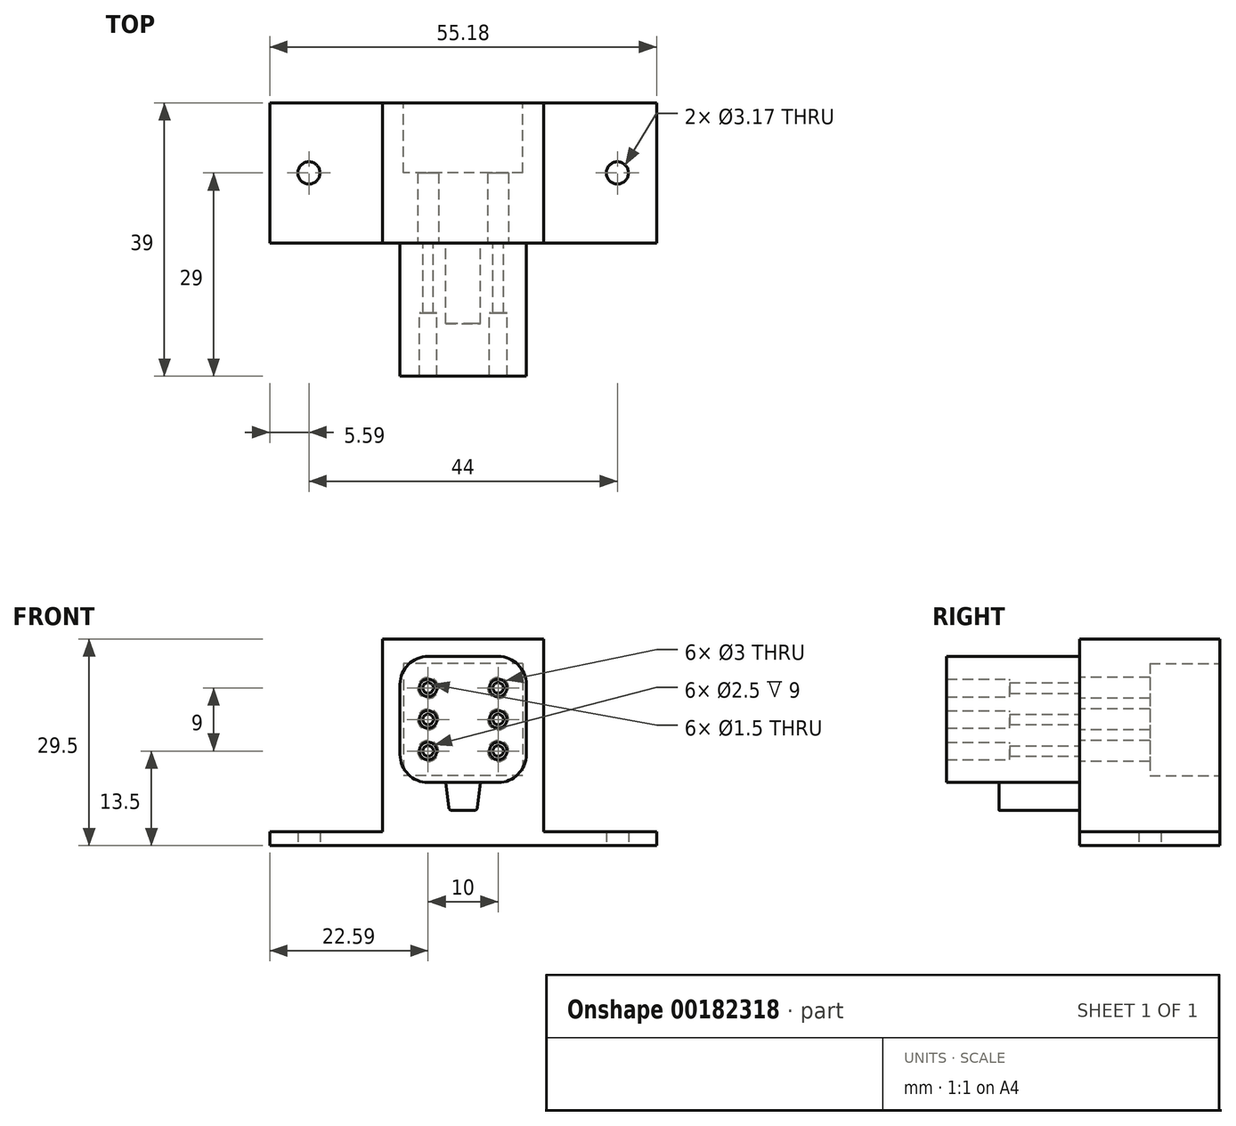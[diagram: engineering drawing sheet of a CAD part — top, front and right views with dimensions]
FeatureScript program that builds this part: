
annotation { "Feature Type Name" : "Feature", "Feature Type Description" : "" }
export const myFeature = defineFeature(function(context is Context, id is Id, definition is map)
    precondition{}
    {
        {
            var Q0;
            Q0=qCreatedBy(makeId("Front.planeOp"),FACE);
            var sketch = newSketch(context, id + "F0", { "sketchPlane" : qUnion([Q0])});
            skLineSegment(sketch, "E0.bottom", {"start": v(7.5, 30.5) * mm, "end": v(17.5, 30.5) * mm});
            skLineSegment(sketch, "E0.top", {"start": v(7.5, 12.5) * mm, "end": v(17.5, 12.5) * mm});
            skLineSegment(sketch, "E0.left", {"start": v(3.5, 26.5) * mm, "end": v(3.5, 16.5) * mm});
            skLineSegment(sketch, "E0.right", {"start": v(21.5, 26.5) * mm, "end": v(21.5, 16.5) * mm});
            skPoint(sketch, "E1.visualSharp", {"position": v(3.5, 30.5) * mm});
            skArc(sketch, "E1.filletArc", {"start": v(7.5, 30.5) * mm, "mid": v(4.67, 29.33) * mm, "end": v(3.5, 26.5) * mm});
            skPoint(sketch, "E2.visualSharp", {"position": v(21.5, 30.5) * mm});
            skArc(sketch, "E2.filletArc", {"start": v(21.5, 26.5) * mm, "mid": v(20.33, 29.33) * mm, "end": v(17.5, 30.5) * mm});
            skPoint(sketch, "E3.visualSharp", {"position": v(21.5, 12.5) * mm});
            skArc(sketch, "E3.filletArc", {"start": v(17.5, 12.5) * mm, "mid": v(20.33, 13.67) * mm, "end": v(21.5, 16.5) * mm});
            skPoint(sketch, "E4.visualSharp", {"position": v(3.5, 12.5) * mm});
            skArc(sketch, "E4.filletArc", {"start": v(3.5, 16.5) * mm, "mid": v(4.67, 13.67) * mm, "end": v(7.5, 12.5) * mm});
            skLineSegment(sketch, "E5", {"start": v(12.5, 30.5) * mm, "end": v(12.5, 6.08) * mm, "construction": true});
            skCircle(sketch, "E6", {"center": v(7.5, 26) * mm, "radius": 1.25 * mm});
            skLineSegment(sketch, "E7", {"start": v(7.5, 26) * mm, "end": v(12.5, 26) * mm, "construction": true});
            skCircle(sketch, "E8.1.0.0", {"center": v(7.5, 21.5) * mm, "radius": 1.25 * mm});
            skCircle(sketch, "E8.2.0.0", {"center": v(7.5, 17) * mm, "radius": 1.25 * mm});
            skLineSegment(sketch, "E8.direction1", {"start": v(7.5, 26) * mm, "end": v(7.5, 21.5) * mm, "construction": true});
            skCircle(sketch, "E9.MirrorC", {"center": v(17.5, 26) * mm, "radius": 1.25 * mm});
            skCircle(sketch, "E10.MirrorC", {"center": v(17.5, 21.5) * mm, "radius": 1.25 * mm});
            skCircle(sketch, "E11.MirrorC", {"center": v(17.5, 17) * mm, "radius": 1.25 * mm});
            skLineSegment(sketch, "E12.MirrorCS", {"start": v(17.5, 26) * mm, "end": v(17.5, 21.5) * mm, "construction": true});
            skSolve(sketch);
        }
        {
            var Q0;
            Q0=qSketchRegion(id+"F0",true);
            extrude(context, id + "F1", {"entities" : qUnion([Q0]), "depth" : 19 * mm});
        }
        {
            var Q0;
            Q0=makeQuery(id+"F1.opExtrude","CAP_FACE",FACE,{"disambiguationData":[OSD([sQuery(id+"F0.wireOp",EDGE,"E0.bottom"),sQuery(id+"F0.wireOp",EDGE,"E0.top"),sQuery(id+"F0.wireOp",EDGE,"E0.left"),sQuery(id+"F0.wireOp",EDGE,"E0.right"),sQuery(id+"F0.wireOp",EDGE,"E1.filletArc"),sQuery(id+"F0.wireOp",EDGE,"E2.filletArc"),sQuery(id+"F0.wireOp",EDGE,"E3.filletArc"),sQuery(id+"F0.wireOp",EDGE,"E4.filletArc"),sQuery(id+"F0.wireOp",EDGE,"6d2e094a-fbc0-4e1c-b2e7-ed02ba3bef07"),sQuery(id+"F0.wireOp",EDGE,"E6"),sQuery(id+"F0.wireOp",EDGE,"E8.1.0.0"),sQuery(id+"F0.wireOp",EDGE,"E8.2.0.0"),sQuery(id+"F0.wireOp",EDGE,"E9.MirrorC"),sQuery(id+"F0.wireOp",EDGE,"E10.MirrorC"),sQuery(id+"F0.wireOp",EDGE,"E11.MirrorC")])],"isStart":true});
            var sketch = newSketch(context, id + "F2", { "sketchPlane" : qUnion([Q0])});
            skLineSegment(sketch, "E13.bottom", {"start": v(-15, 12.5) * mm, "end": v(-10, 12.5) * mm});
            skPoint(sketch, "E14", {"position": v(-12.5, 12.5) * mm});
            skLineSegment(sketch, "E15", {"start": v(-15, 12.5) * mm, "end": v(-14.55, 8.94) * mm});
            skLineSegment(sketch, "E16", {"start": v(-14.06, 8.5) * mm, "end": v(-10.94, 8.5) * mm});
            skLineSegment(sketch, "E17", {"start": v(-10.45, 8.94) * mm, "end": v(-10, 12.5) * mm});
            skLineSegment(sketch, "E18", {"start": v(-12.5, 8.5) * mm, "end": v(-12.5, 12.5) * mm, "construction": true});
            skPoint(sketch, "E19.visualSharp", {"position": v(-14.5, 8.5) * mm});
            skArc(sketch, "E19.filletArc", {"start": v(-14.55, 8.94) * mm, "mid": v(-14.39, 8.63) * mm, "end": v(-14.06, 8.5) * mm});
            skPoint(sketch, "E20.visualSharp", {"position": v(-10.5, 8.5) * mm});
            skArc(sketch, "E20.filletArc", {"start": v(-10.94, 8.5) * mm, "mid": v(-10.61, 8.63) * mm, "end": v(-10.45, 8.94) * mm});
            skSolve(sketch);
        }
        {
            var Q0;
            Q0=qSketchRegion(id+"F2",true);
            extrude(context, id + "F3", {"entities" : qUnion([Q0]), "operationType" : NewBodyOperationType.ADD, "oppositeDirection" : true, "depth" : 11.5 * mm});
        }
        {
            var Q0;
            Q0=makeQuery(id+"F3.boolean.opBoolean","MERGE",FACE,{"derivedFrom":[makeQuery(id+"F1.opExtrude","CAP_FACE",FACE,{"disambiguationData":[OSD([sQuery(id+"F0.wireOp",EDGE,"E0.bottom"),sQuery(id+"F0.wireOp",EDGE,"E0.top"),sQuery(id+"F0.wireOp",EDGE,"E0.left"),sQuery(id+"F0.wireOp",EDGE,"E0.right"),sQuery(id+"F0.wireOp",EDGE,"E1.filletArc"),sQuery(id+"F0.wireOp",EDGE,"E2.filletArc"),sQuery(id+"F0.wireOp",EDGE,"E3.filletArc"),sQuery(id+"F0.wireOp",EDGE,"E4.filletArc"),sQuery(id+"F0.wireOp",EDGE,"6d2e094a-fbc0-4e1c-b2e7-ed02ba3bef07"),sQuery(id+"F0.wireOp",EDGE,"E6"),sQuery(id+"F0.wireOp",EDGE,"E8.1.0.0"),sQuery(id+"F0.wireOp",EDGE,"E8.2.0.0"),sQuery(id+"F0.wireOp",EDGE,"E9.MirrorC"),sQuery(id+"F0.wireOp",EDGE,"E10.MirrorC"),sQuery(id+"F0.wireOp",EDGE,"E11.MirrorC")])],"isStart":true}),makeQuery(id+"F3.opExtrude","CAP_FACE",FACE,{"disambiguationData":[OSD([sQuery(id+"F2.wireOp",EDGE,"E13.bottom"),sQuery(id+"F2.wireOp",EDGE,"E15"),sQuery(id+"F2.wireOp",EDGE,"E16"),sQuery(id+"F2.wireOp",EDGE,"E17"),sQuery(id+"F2.wireOp",EDGE,"E19.filletArc"),sQuery(id+"F2.wireOp",EDGE,"E20.filletArc")])],"isStart":true})]});
            var sketch = newSketch(context, id + "F4", { "sketchPlane" : qUnion([Q0])});
            skCircle(sketch, "E21", {"center": v(-17.5, 26) * mm, "radius": 0.75 * mm});
            skCircle(sketch, "E22", {"center": v(-17.5, 21.5) * mm, "radius": 0.75 * mm});
            skCircle(sketch, "E23", {"center": v(-17.5, 17) * mm, "radius": 0.75 * mm});
            skCircle(sketch, "E24", {"center": v(-7.5, 17) * mm, "radius": 0.75 * mm});
            skCircle(sketch, "E25", {"center": v(-7.5, 21.5) * mm, "radius": 0.75 * mm});
            skCircle(sketch, "E26", {"center": v(-7.5, 26) * mm, "radius": 0.75 * mm});
            skCircle(sketch, "E27.0", {"center": v(-17.5, 26) * mm, "radius": 1.25 * mm});
            skCircle(sketch, "E27.1", {"center": v(-7.5, 26) * mm, "radius": 1.25 * mm});
            skCircle(sketch, "E27.2", {"center": v(-7.5, 21.5) * mm, "radius": 1.25 * mm});
            skCircle(sketch, "E27.3", {"center": v(-7.5, 17) * mm, "radius": 1.25 * mm});
            skCircle(sketch, "E27.4", {"center": v(-17.5, 17) * mm, "radius": 1.25 * mm});
            skCircle(sketch, "E27.5", {"center": v(-17.5, 21.5) * mm, "radius": 1.25 * mm});
            skSolve(sketch);
        }
        {
            var Q0;
            Q0 = qSketchRegion(id + "F4", true);
            extrude(context, id + "F5", {"entities" : qUnion([Q0]), "operationType" : NewBodyOperationType.ADD, "oppositeDirection" : true, "depth" : 10 * mm});
        }
        {
            var Q0;
            Q0=makeQuery(id+"F0vBC64rinZp2fi_1.boolean.opBoolean","MERGE",FACE,{"derivedFrom":[makeQuery(id+"F1.opExtrude","CAP_FACE",FACE,{"disambiguationData":[OSD([sQuery(id+"F0.wireOp",EDGE,"E0.bottom"),sQuery(id+"F0.wireOp",EDGE,"E0.top"),sQuery(id+"F0.wireOp",EDGE,"E0.left"),sQuery(id+"F0.wireOp",EDGE,"E0.right"),sQuery(id+"F0.wireOp",EDGE,"E1.filletArc"),sQuery(id+"F0.wireOp",EDGE,"E2.filletArc"),sQuery(id+"F0.wireOp",EDGE,"E3.filletArc"),sQuery(id+"F0.wireOp",EDGE,"E4.filletArc"),sQuery(id+"F0.wireOp",EDGE,"6d2e094a-fbc0-4e1c-b2e7-ed02ba3bef07"),sQuery(id+"F0.wireOp",EDGE,"E6"),sQuery(id+"F0.wireOp",EDGE,"E8.1.0.0"),sQuery(id+"F0.wireOp",EDGE,"E8.2.0.0"),sQuery(id+"F0.wireOp",EDGE,"E9.MirrorC"),sQuery(id+"F0.wireOp",EDGE,"E10.MirrorC"),sQuery(id+"F0.wireOp",EDGE,"E11.MirrorC")])],"isStart":true}),makeQuery(id+"F0vBC64rinZp2fi_1.opExtrude","CAP_FACE",FACE,{"disambiguationData":[OSD([sQuery(id+"FvWWqIlKoH8mqQo_1.wireOp",EDGE,"c2f8d72c-7963-432e-be51-951a3f4c488a"),sQuery(id+"FvWWqIlKoH8mqQo_1.wireOp",EDGE,"O0sRqyTz-9wY0-XlkF-kKeY-Mwcwz92cmgjL")])],"isStart":true}),makeQuery(id+"F0vBC64rinZp2fi_1.opExtrude","CAP_FACE",FACE,{"disambiguationData":[OSD([sQuery(id+"FvWWqIlKoH8mqQo_1.wireOp",EDGE,"7cdc9034-cf40-4037-8061-822d9703f2a8.1.0.0"),sQuery(id+"FvWWqIlKoH8mqQo_1.wireOp",EDGE,"a965afdf-efe5-46a0-92df-f40ea41c0fde.1.0.0")])],"isStart":true}),makeQuery(id+"F0vBC64rinZp2fi_1.opExtrude","CAP_FACE",FACE,{"disambiguationData":[OSD([sQuery(id+"FvWWqIlKoH8mqQo_1.wireOp",EDGE,"7cdc9034-cf40-4037-8061-822d9703f2a8.2.0.0"),sQuery(id+"FvWWqIlKoH8mqQo_1.wireOp",EDGE,"a965afdf-efe5-46a0-92df-f40ea41c0fde.2.0.0")])],"isStart":true}),makeQuery(id+"F0vBC64rinZp2fi_1.opExtrude","CAP_FACE",FACE,{"disambiguationData":[OSD([sQuery(id+"FvWWqIlKoH8mqQo_1.wireOp",EDGE,"6b83606b-9192-4265-a1d3-858796a49a93.MirrorC"),sQuery(id+"FvWWqIlKoH8mqQo_1.wireOp",EDGE,"e7e7a0de-6a7c-4f06-b9dd-4dd7a93f13140.MirrorC")])],"isStart":true}),makeQuery(id+"F0vBC64rinZp2fi_1.opExtrude","CAP_FACE",FACE,{"disambiguationData":[OSD([sQuery(id+"FvWWqIlKoH8mqQo_1.wireOp",EDGE,"99da94c0-a4cd-44c7-8ef6-46f96fbd6392.MirrorC"),sQuery(id+"FvWWqIlKoH8mqQo_1.wireOp",EDGE,"0ea93e25-ebf9-4499-be77-ca466537f80e0.MirrorC")])],"isStart":true}),makeQuery(id+"F0vBC64rinZp2fi_1.opExtrude","CAP_FACE",FACE,{"disambiguationData":[OSD([sQuery(id+"FvWWqIlKoH8mqQo_1.wireOp",EDGE,"935e3073-f986-4d4d-a348-27eb769d3106.MirrorC"),sQuery(id+"FvWWqIlKoH8mqQo_1.wireOp",EDGE,"0b4c3d06-249c-409a-8747-af57adffb9380.MirrorC")])],"isStart":true})]});
            var sketch = newSketch(context, id + "F6", { "sketchPlane" : qUnion([Q0])});
            skLineSegment(sketch, "E28", {"start": v(-12.5, 24.17) * mm, "end": v(-12.5, 6.17) * mm, "construction": true});
            skCircle(sketch, "E29", {"center": v(-17.5, 26) * mm, "radius": 1.5 * mm});
            skLineSegment(sketch, "E30", {"start": v(-17.5, 26) * mm, "end": v(-12.5, 26) * mm, "construction": true});
            skCircle(sketch, "E31.1.0.0", {"center": v(-17.5, 21.5) * mm, "radius": 1.5 * mm});
            skCircle(sketch, "E31.2.0.0", {"center": v(-17.5, 17) * mm, "radius": 1.5 * mm});
            skLineSegment(sketch, "E31.direction1", {"start": v(-17.5, 26) * mm, "end": v(-17.5, 21.5) * mm, "construction": true});
            skCircle(sketch, "E32.MirrorC", {"center": v(-7.5, 26) * mm, "radius": 1.5 * mm});
            skCircle(sketch, "E33.MirrorC", {"center": v(-7.5, 21.5) * mm, "radius": 1.5 * mm});
            skCircle(sketch, "E34.MirrorC", {"center": v(-7.5, 17) * mm, "radius": 1.5 * mm});
            skLineSegment(sketch, "E35.MirrorCS", {"start": v(-7.5, 26) * mm, "end": v(-7.5, 21.5) * mm, "construction": true});
            skLineSegment(sketch, "E36.0", {"start": v(-24, 33) * mm, "end": v(-1, 33) * mm});
            skLineSegment(sketch, "E36.1", {"start": v(-24, 33) * mm, "end": v(-24, 3.5) * mm});
            skLineSegment(sketch, "E36.2", {"start": v(-24, 3.5) * mm, "end": v(-1, 3.5) * mm});
            skLineSegment(sketch, "E36.3", {"start": v(-1, 33) * mm, "end": v(-1, 3.5) * mm});
            skSolve(sketch);
        }
        {
            var Q0;
            Q0 = qSketchRegion(id + "F6", true);
            extrude(context, id + "F7", {"entities" : qUnion([Q0]), "depth" : 20 * mm});
        }
        {
            var Q0;
            Q0=makeQuery(id+"F7.opExtrude","SWEPT_FACE",FACE,{"disambiguationData":[OSD([sQuery(id+"F6.wireOp",EDGE,"E36.2")])]});
            var sketch = newSketch(context, id + "F8", { "sketchPlane" : qUnion([Q0])});
            skLineSegment(sketch, "E37.bottom", {"start": v(40.09, 0) * mm, "end": v(24, 0) * mm});
            skLineSegment(sketch, "E37.top", {"start": v(40.09, -20) * mm, "end": v(-15.09, -20) * mm});
            skLineSegment(sketch, "E37.left", {"start": v(40.09, 0) * mm, "end": v(40.09, -20) * mm});
            skLineSegment(sketch, "E37.right", {"start": v(-15.09, 0) * mm, "end": v(-15.09, -20) * mm});
            skPoint(sketch, "E38.centerSnap0", {"position": v(40.09, -10) * mm});
            skPoint(sketch, "E39.centerSnap0", {"position": v(-15.09, -10) * mm});
            skLineSegment(sketch, "E40", {"start": v(12.5, 0) * mm, "end": v(12.5, -20) * mm, "construction": true});
            skCircle(sketch, "E41", {"center": v(34.5, -10) * mm, "radius": 1.59 * mm});
            skCircle(sketch, "E42.MirrorC", {"center": v(-9.5, -10) * mm, "radius": 1.59 * mm});
            skLineSegment(sketch, "E43", {"start": v(1, -20) * mm, "end": v(1, 0) * mm});
            skLineSegment(sketch, "E44", {"start": v(24, -20) * mm, "end": v(24, 0) * mm});
            skLineSegment(sketch, "E45.trimOffspring", {"start": v(1, 0) * mm, "end": v(-15.09, 0) * mm});
            skSolve(sketch);
        }
        {
            var Q0;
            Q0 = qSketchRegion(id + "F8", true);
            extrude(context, id + "F9", {"entities" : qUnion([Q0]), "operationType" : NewBodyOperationType.ADD, "oppositeDirection" : true, "depth" : 2 * mm});
        }
        {
            var Q0;
            Q0=makeQuery(id+"F9.boolean.opBoolean","MERGE",FACE,{"derivedFrom":[makeQuery(id+"F7.opExtrude","CAP_FACE",FACE,{"disambiguationData":[OSD([sQuery(id+"F6.wireOp",EDGE,"228e9027-ee7f-4dd7-b60f-f69f1eade7ae"),sQuery(id+"F6.wireOp",EDGE,"E29"),sQuery(id+"F6.wireOp",EDGE,"E31.1.0.0"),sQuery(id+"F6.wireOp",EDGE,"E31.2.0.0"),sQuery(id+"F6.wireOp",EDGE,"E32.MirrorC"),sQuery(id+"F6.wireOp",EDGE,"E33.MirrorC"),sQuery(id+"F6.wireOp",EDGE,"E34.MirrorC"),sQuery(id+"F6.wireOp",EDGE,"E36.0"),sQuery(id+"F6.wireOp",EDGE,"E36.1"),sQuery(id+"F6.wireOp",EDGE,"E36.2"),sQuery(id+"F6.wireOp",EDGE,"E36.3")])],"isStart":false}),makeQuery(id+"F9.opExtrude","SWEPT_FACE",FACE,{"disambiguationData":[OSD([sQuery(id+"F8.wireOp",EDGE,"E37.top")])]})]});
            var sketch = newSketch(context, id + "F10", { "sketchPlane" : qUnion([Q0])});
            skLineSegment(sketch, "E46.bottom", {"start": v(-21, 29.5) * mm, "end": v(-4, 29.5) * mm});
            skLineSegment(sketch, "E46.top", {"start": v(-21, 13.5) * mm, "end": v(-4, 13.5) * mm});
            skLineSegment(sketch, "E46.left", {"start": v(-21, 29.5) * mm, "end": v(-21, 13.5) * mm});
            skLineSegment(sketch, "E46.right", {"start": v(-4, 29.5) * mm, "end": v(-4, 13.5) * mm});
            skSolve(sketch);
        }
        {
            var Q0;
            Q0 = qSketchRegion(id + "F10", true);
            extrude(context, id + "F11", {"entities" : qUnion([Q0]), "operationType" : NewBodyOperationType.REMOVE, "oppositeDirection" : true, "depth" : 10 * mm});
        }
    });
